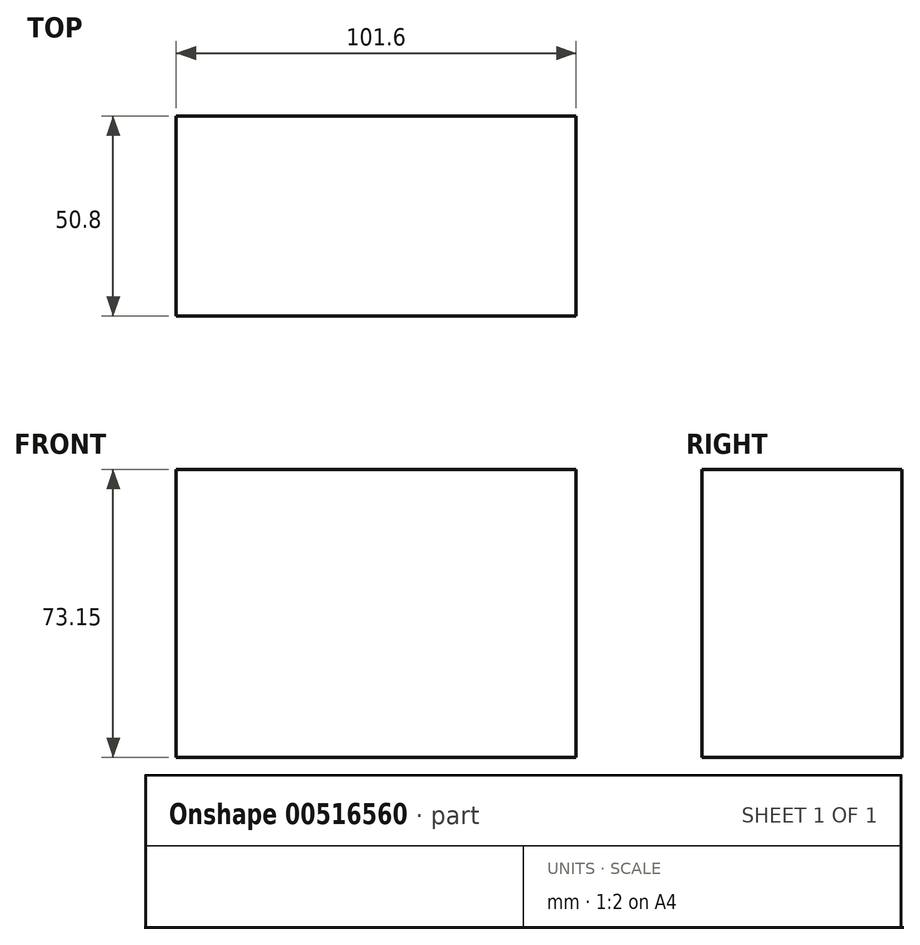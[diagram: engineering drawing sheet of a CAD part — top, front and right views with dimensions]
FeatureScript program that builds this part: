
annotation { "Feature Type Name" : "Feature", "Feature Type Description" : "" }
export const myFeature = defineFeature(function(context is Context, id is Id, definition is map)
    precondition{}
    {
        {
            var Q0;
            Q0=qCreatedBy(makeId("Top.planeOp"),FACE);
            var sketch = newSketch(context, id + "F0", { "sketchPlane" : qUnion([Q0])});
            skLineSegment(sketch, "E0.bottom", {"start": v(-50.8, -25.4) * mm, "end": v(50.8, -25.4) * mm});
            skLineSegment(sketch, "E0.top", {"start": v(-50.8, 25.4) * mm, "end": v(50.8, 25.4) * mm});
            skLineSegment(sketch, "E0.left", {"start": v(-50.8, -25.4) * mm, "end": v(-50.8, 25.4) * mm});
            skLineSegment(sketch, "E0.right", {"start": v(50.8, -25.4) * mm, "end": v(50.8, 25.4) * mm});
            skSolve(sketch);
        }
        {
            var Q0;
            Q0 = qSketchRegion(id + "F0", true);
            extrude(context, id + "F1", {"entities" : qUnion([Q0]), "depth" : 73.15 * mm, "offsetDistance" : 25.4 * mm});
        }
    });
